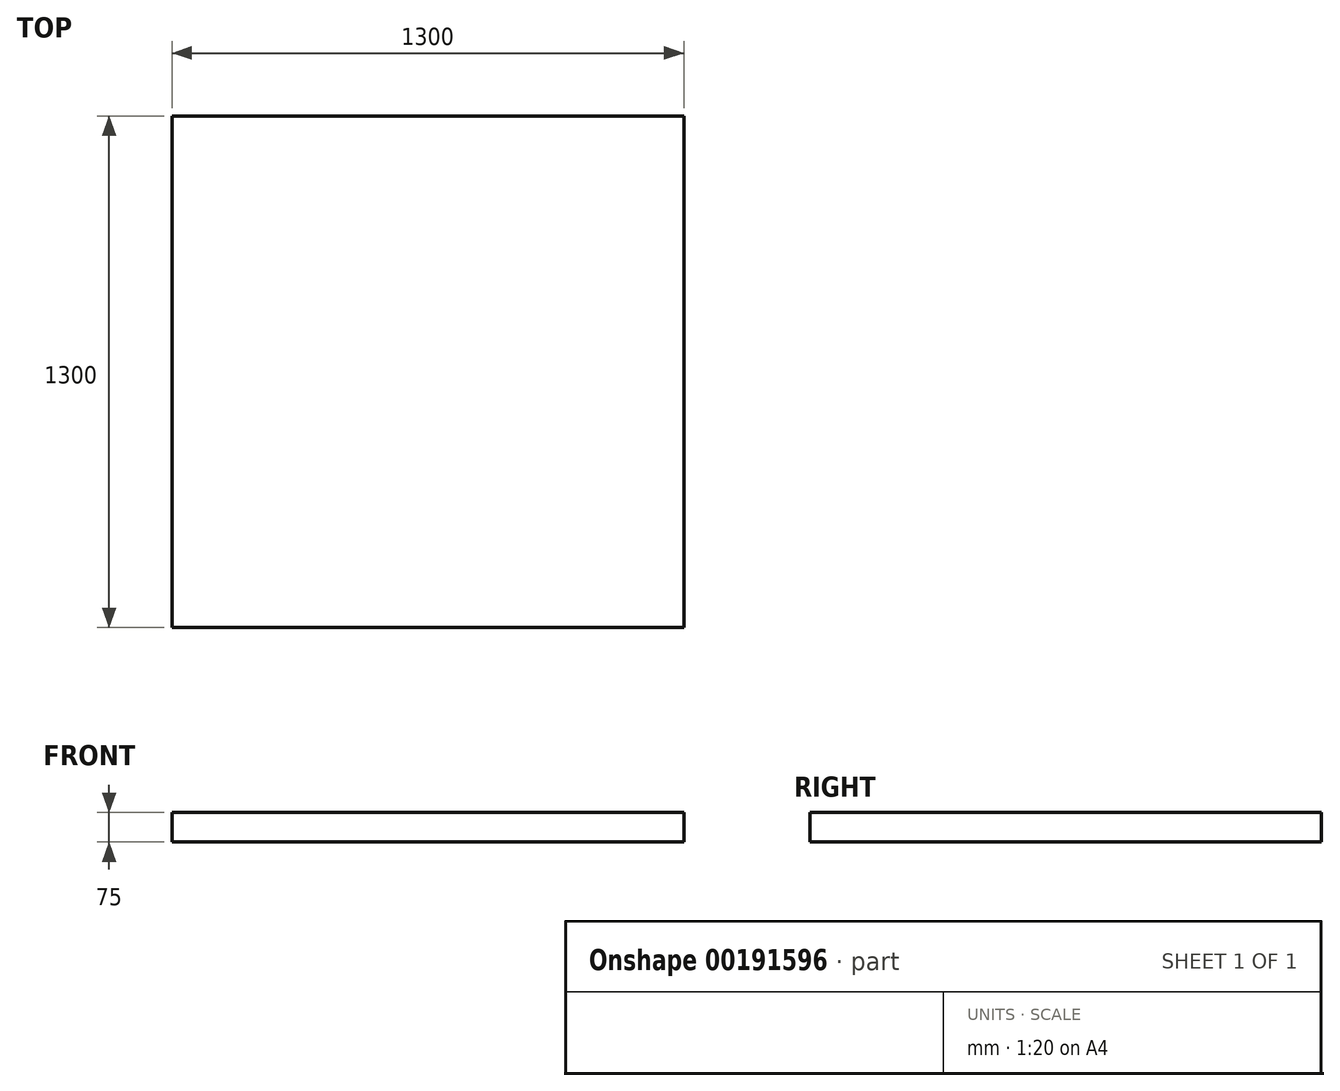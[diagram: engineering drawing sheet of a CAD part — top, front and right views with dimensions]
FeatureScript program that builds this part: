
annotation { "Feature Type Name" : "Feature", "Feature Type Description" : "" }
export const myFeature = defineFeature(function(context is Context, id is Id, definition is map)
    precondition{}
    {
        {
            var Q0;
            Q0=qCreatedBy(makeId("Top.planeOp"),FACE);
            var sketch = newSketch(context, id + "F0", { "sketchPlane" : qUnion([Q0])});
            skLineSegment(sketch, "E0.bottom", {"start": v(-650, -650) * mm, "end": v(650, -650) * mm});
            skLineSegment(sketch, "E0.top", {"start": v(-650, 650) * mm, "end": v(650, 650) * mm});
            skLineSegment(sketch, "E0.left", {"start": v(-650, 650) * mm, "end": v(-650, -650) * mm});
            skLineSegment(sketch, "E0.right", {"start": v(650, 650) * mm, "end": v(650, -650) * mm});
            skLineSegment(sketch, "E1", {"start": v(-650, -650) * mm, "end": v(650, 650) * mm, "construction": true});
            skLineSegment(sketch, "E2", {"start": v(-650, 650) * mm, "end": v(650, -650) * mm, "construction": true});
            skSolve(sketch);
        }
        {
            var Q0;
            Q0=qSketchRegion(id+"F0",true);
            extrude(context, id + "F1", {"entities" : qUnion([Q0]), "depth" : 75 * mm});
        }
    });
